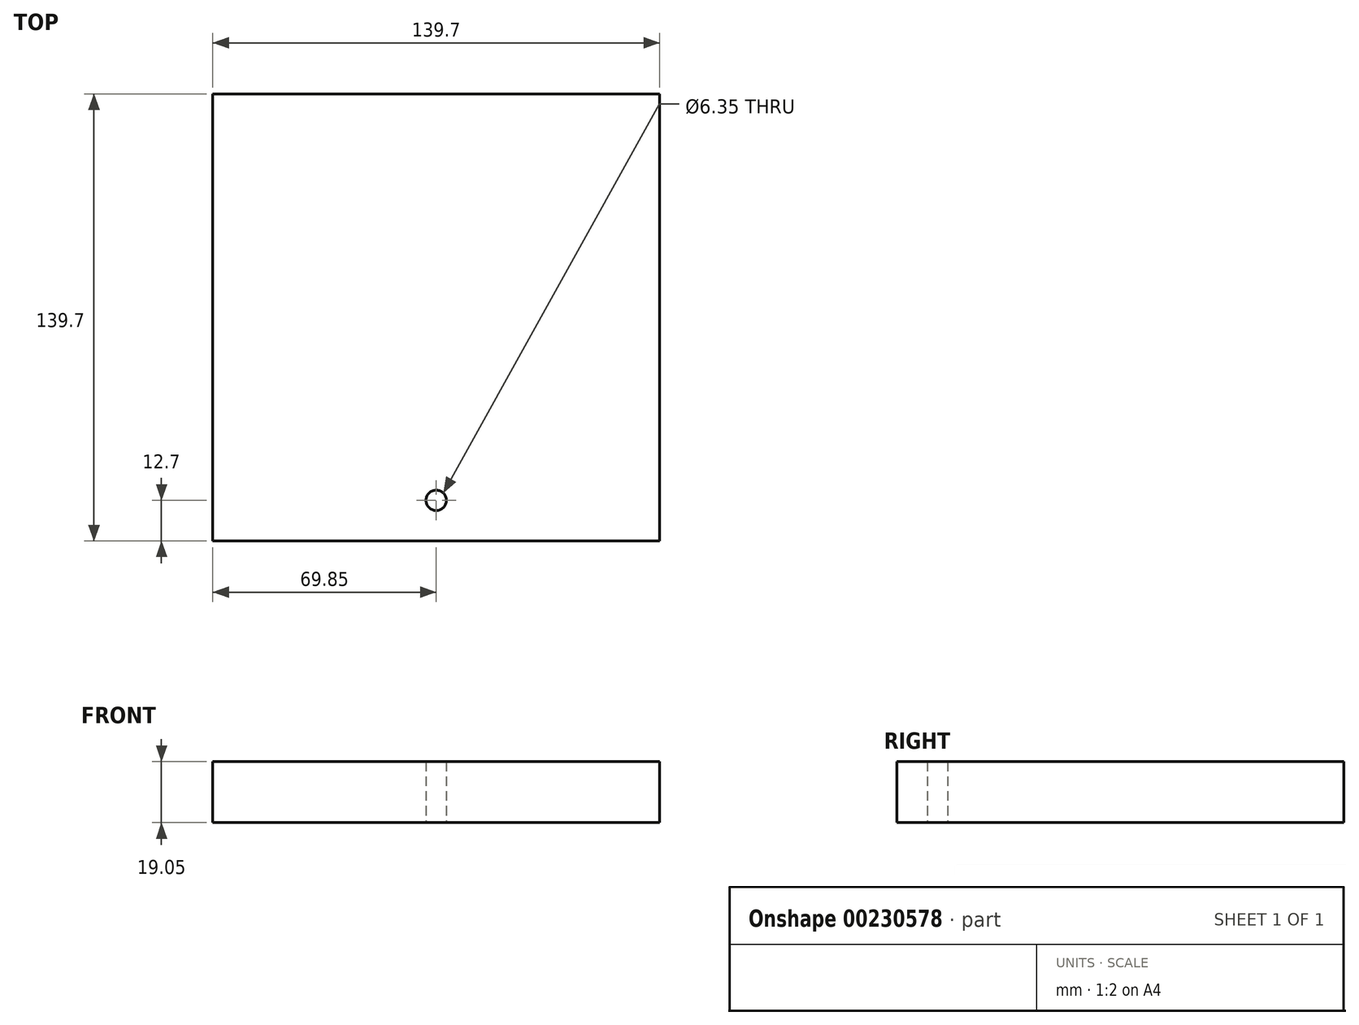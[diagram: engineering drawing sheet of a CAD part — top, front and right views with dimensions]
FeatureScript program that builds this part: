
annotation { "Feature Type Name" : "Feature", "Feature Type Description" : "" }
export const myFeature = defineFeature(function(context is Context, id is Id, definition is map)
    precondition{}
    {
        {
            var Q0;
            Q0=qCreatedBy(makeId("Top.planeOp"),FACE);
            var sketch = newSketch(context, id + "F0", { "sketchPlane" : qUnion([Q0])});
            skLineSegment(sketch, "E0.bottom", {"start": v(-69.85, -69.85) * mm, "end": v(69.85, -69.85) * mm});
            skLineSegment(sketch, "E0.top", {"start": v(-69.85, 69.85) * mm, "end": v(69.85, 69.85) * mm});
            skLineSegment(sketch, "E0.left", {"start": v(-69.85, -69.85) * mm, "end": v(-69.85, 69.85) * mm});
            skLineSegment(sketch, "E0.right", {"start": v(69.85, -69.85) * mm, "end": v(69.85, 69.85) * mm});
            skPoint(sketch, "E0.middle", {"position": v(0, 0) * mm});
            skLineSegment(sketch, "E1", {"start": v(0, -69.85) * mm, "end": v(0, -57.15) * mm});
            skPoint(sketch, "E1.endSnap0", {"position": v(0, -69.85) * mm});
            skCircle(sketch, "E2", {"center": v(0, -57.15) * mm, "radius": 3.18 * mm});
            skSolve(sketch);
        }
        {
            var Q0;
            Q0 = qSketchRegion(id + "F0", true);
            extrude(context, id + "F1", {"entities" : qUnion([Q0]), "depth" : 19.05 * mm});
        }
    });
